# Revit family: Plumbing-Valves-Sloan-REGAL-110-XLz
name_source: partatom
category: Plumbing Fixtures
units: mm (PartAtom-declared; Revit-internal decimal feet)

## family parameters
Cut with Voids When Loaded = No
Host = Face
OmniClass Number = 23.45.05.14.99
OmniClass Title = Other Sanitary Washing Plumbing Fixtures
Part Type = Normal
Room Calculation Point = No
Round Connector Dimension = Use Diameter
Shared = No

## types (7) — shared parameters
Assembly Code = D2020300
CW Connection = Yes
Centerline of Supply from Top of Fixture = 11 1/2"
Centerline of Supply to Centerline of Valve = 4 3/4"
Default Elevation = 0"
Edition number = 1
HW Connection = No
Height = 13 1/2"
Keynote = 15410
Manufacturer = Sloan Valve
Operating Water Pressure = 15 – 80 PSI (103 – 552 kPa)
Product Material = Sloan Valve - Finish - Polished Chrome
Product data url = https://www.bimobject.com
URL = www.sloanvalve.com
Valve Pressure Drop = 0.00 psi
Vent Connection = No
Waste Connection = No
Water Inlet Connection Diameter = 1"
zero-valued in all types: CWFU, HWFU, WFU

## per-type parameters (varying)
| type | Description | Flush Rate | Part Number |
| REGAL 110-2.4-XL | 2.4 gpf, XL Sweat Solder Adapter Kit, Polished Chrome Finish, Fixture
Connection Top Spud, Single Flush, Regal® Exposed Manual Water
Closet Flushometer. | 2.4 gpf (9.1 Lpf) | 3980063 |
| REGAL 110-3.5-XL | 3.5 gpf, XL Sweat Solder Adapter Kit, Polished Chrome Finish, Fixture
Connection Top Spud, Single Flush, Regal® Exposed Manual Water
Closet Flushometer. | 3.5 gpf (13.2 Lpf) | 3080153 |
| REGAL 110-3.5-YO | 3.5 gpf, Angle Stop Bumper, Polished Chrome Finish, Fixture
Connection Top Spud, Single Flush, Regal® Exposed Manual Water
Closet Flushometer. | 3.5 gpf (13.2 Lpf) | 3980009 |
| REGAL 110-3.5-U | 3.5 gpf, Polished Chrome Finish, 1.25" Flush Connection, Fixture
Connection Top Spud, Single Flush, Regal® Exposed Manual Water
Closet Flushometer. | 3.5 gpf (13.2 Lpf) | 3980122 |
| REGAL 110-3.5-XYV | 3.5 gpf, Polished Chrome Finish, Fixture Connection Top Spud, Single
Flush, Less Vacuum Breaker, Regal® Exposed Manual Water Closet
Flushometer. | 3.5 gpf (13.2 Lpf) | 3980080 |
| REGAL 110-2.4-L/STOP | 2.4 gpf, Polished Chrome Finish, Fixture Connection Top Spud, Single
Flush, Less Control Stop, Regal® Exposed Manual Water Closet
Flushometer. | 2.4 gpf (9.1 Lpf) | 3980083 |
| REGAL 110-3.5-TP | 3.5 gpf, Polished Chrome Finish, Fixture Connection Top Spud, Single
Flush, Trap Primer Outlet Tube, Regal® Exposed Manual Water Closet
Flushometer. | 3.5 gpf (13.2 Lpf) | 3980016 |

note: column(s) folded — value = type name in every type: Model

## geometry (parser evidence)
native form markers: Sweep x4
no freeform markers — native parametric forms only
